# Revit family: Shower-Shower_Door-STERLING-Intrigue-SP2270A
name_source: partatom
category: Specialty Equipment
revit_build: Autodesk Revit 2015 (Build: 20140606_1530(x64)
units: mm (PartAtom-declared; Revit-internal decimal feet)

## types (1)
- S-Silver Frame Finish with Pebbled Glass Texture
    ADA Compliant = No
    Assembly Code = C1030200
    Date Modified = 06/20/2019
    Default Elevation = 0"
    Description = Framed Neo-Angle Corner Shower Door 15-13/16 inch x 27-9/16 inch x 15-13/16 inch x 72 inch Hr
    Finish = Sterling-Metal-S-Silver
    Height = 72"
    Length = 27 9/16"
    Manufacturer = KOHLER Co.
    MasterFormat 1995 = 10820
    MasterFormat 2004 = 10.28.13
    Material = Anodized Aluminum
    Model = SP2270A-38S
    Product Documentation Link = https://resources.kohler.com
    Product Name = Intrigue
    Product Page URL = http://www.sterlingplumbing.com
    URL = https://www.sterlingplumbing.com
https://www.sterlingplumbing.com
    WaterSense Certified = No
    Width = 15 13/16"

## geometry (parser evidence)
native form markers: Sweep x8
no freeform markers — native parametric forms only
